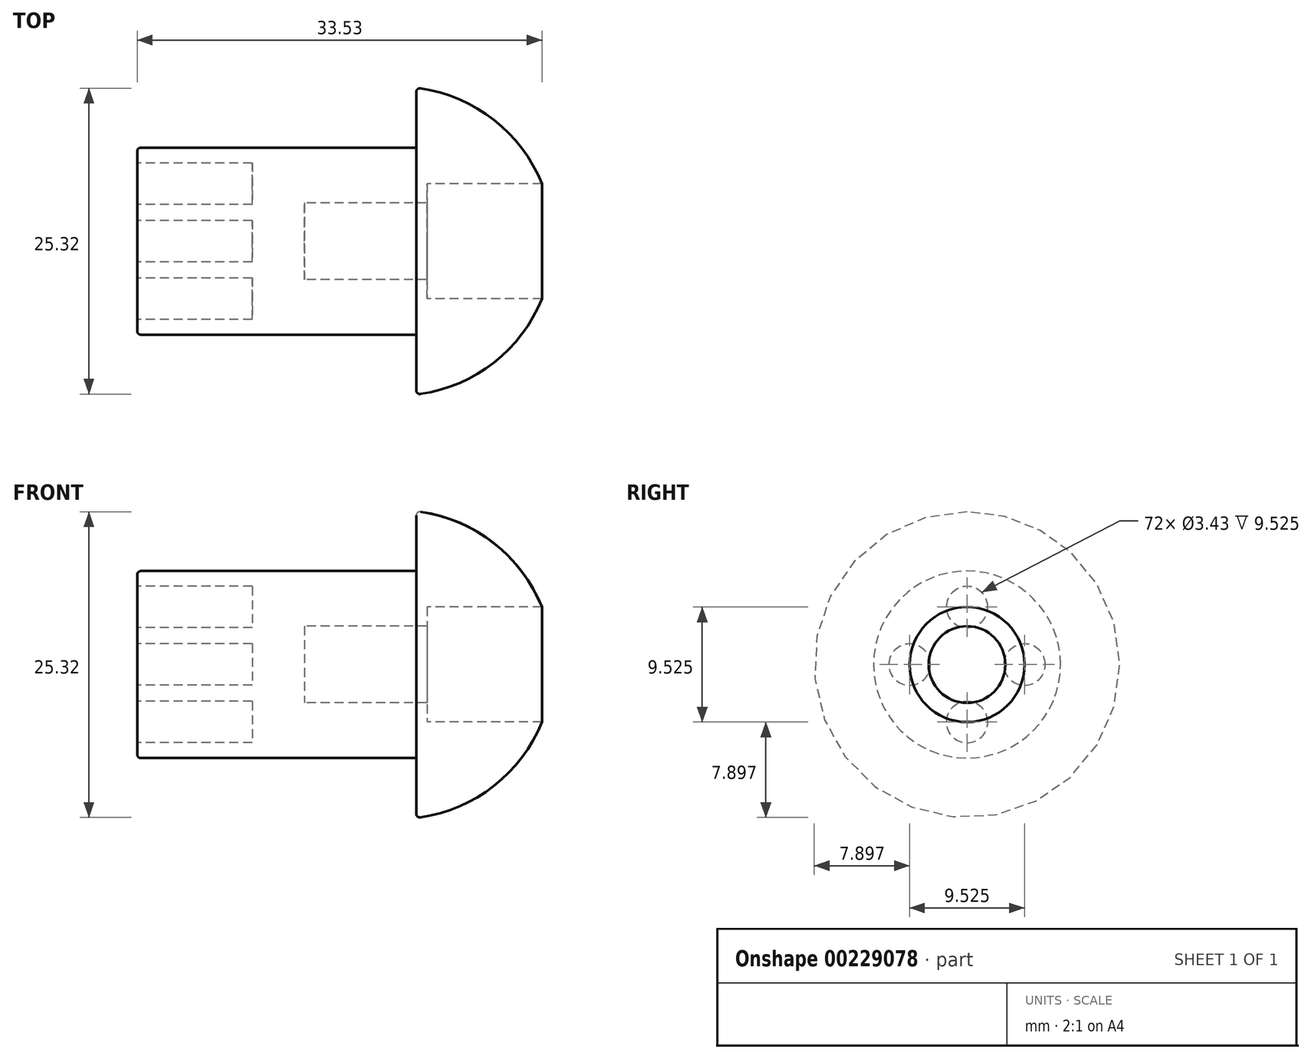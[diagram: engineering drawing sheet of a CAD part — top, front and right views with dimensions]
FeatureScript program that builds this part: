
annotation { "Feature Type Name" : "Feature", "Feature Type Description" : "" }
export const myFeature = defineFeature(function(context is Context, id is Id, definition is map)
    precondition{}
    {
        {
            var Q0;
            Q0=qCreatedBy(makeId("Front.planeOp"),FACE);
            var sketch = newSketch(context, id + "F0", { "sketchPlane" : qUnion([Q0])});
            skLineSegment(sketch, "E0", {"start": v(0, 0) * mm, "end": v(0, 7.75) * mm});
            skLineSegment(sketch, "E1", {"start": v(0, 7.75) * mm, "end": v(23.11, 7.75) * mm});
            skLineSegment(sketch, "E2", {"start": v(23.11, 7.75) * mm, "end": v(23.11, 12.7) * mm});
            skLineSegment(sketch, "E3", {"start": v(0, 0) * mm, "end": v(13.84, 0) * mm});
            skLineSegment(sketch, "E4", {"start": v(33.53, 4.76) * mm, "end": v(24, 4.76) * mm});
            skLineSegment(sketch, "E5", {"start": v(24, 4.76) * mm, "end": v(24, 3.17) * mm});
            skLineSegment(sketch, "E6", {"start": v(24, 3.17) * mm, "end": v(13.84, 3.17) * mm});
            skLineSegment(sketch, "E7", {"start": v(13.84, 3.17) * mm, "end": v(13.84, 0) * mm});
            skArc(sketch, "E8", {"start": v(33.53, 4.76) * mm, "mid": v(29.41, 10.17) * mm, "end": v(23.11, 12.7) * mm});
            skPoint(sketch, "E9.end.orphan", {"position": v(30.27, 12.7) * mm});
            skPoint(sketch, "E10.orphan", {"position": v(33.53, 12.7) * mm});
            skPoint(sketch, "E11.orphan", {"position": v(23.11, 0) * mm});
            skPoint(sketch, "E12.orphan", {"position": v(24, 0) * mm});
            skSolve(sketch);
        }
        {
            var Q0;
            Q0 = qSketchRegion(id + "F0", true);
            var Q1;
            Q1=sQuery(id+"F0.wireOp",EDGE,"E3");
            revolve(context, id + "F1", {"entities" : qUnion([Q0]), "axis" : qUnion([Q1]), "revolveType" : RevolveType.FULL});
        }
        {
            var Q0;
            Q0=makeQuery(id+"F1.opRevolve","SWEPT_FACE",FACE,{"disambiguationData":[OSD([sQuery(id+"F0.wireOp",EDGE,"E0")])]});
            var sketch = newSketch(context, id + "F2", { "sketchPlane" : qUnion([Q0])});
            skCircle(sketch, "E13", {"center": v(0, 4.76) * mm, "radius": 1.71 * mm});
            skCircle(sketch, "E14", {"center": v(4.76, 0) * mm, "radius": 1.71 * mm});
            skCircle(sketch, "E15", {"center": v(0, -4.76) * mm, "radius": 1.71 * mm});
            skCircle(sketch, "E16", {"center": v(-4.76, 0) * mm, "radius": 1.71 * mm});
            skSolve(sketch);
        }
        {
            var Q0;
            Q0 = qSketchRegion(id + "F2", true);
            extrude(context, id + "F3", {"entities" : qUnion([Q0]), "operationType" : NewBodyOperationType.REMOVE, "oppositeDirection" : true, "depth" : 9.52 * mm});
        }
        {
            var Q0;
            Q0=makeQuery(id+"F1.opRevolve","SWEPT_EDGE",EDGE,{"disambiguationData":[OSD([sQuery(id+"F0.wireOp",EDGE,"E0"),sQuery(id+"F0.wireOp",EDGE,"E1")])]});
            var Q1;
            Q1=makeQuery(id+"F1.opRevolve","SWEPT_EDGE",EDGE,{"disambiguationData":[OSD([sQuery(id+"F0.wireOp",EDGE,"E2"),sQuery(id+"F0.wireOp",EDGE,"E8")])]});
            fillet(context, id + "F4", {"entities" : qUnion([Q0, Q1]), "radius" : 0.3 * mm, "tangentPropagation" : true, "allowEdgeOverflow" : false});
        }
    });
